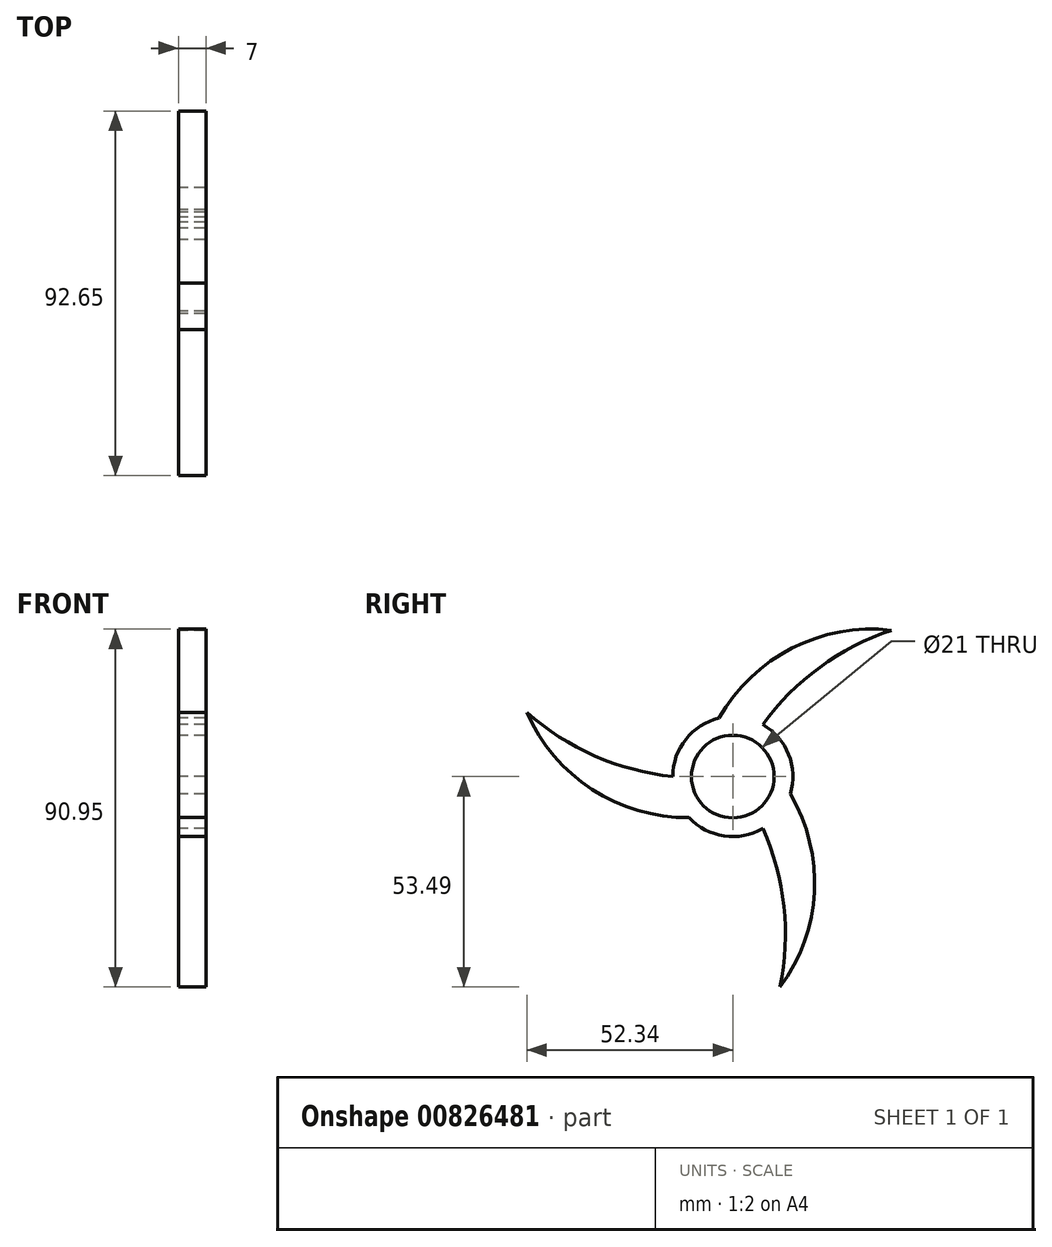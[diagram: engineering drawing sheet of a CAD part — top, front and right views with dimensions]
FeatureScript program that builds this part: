
annotation { "Feature Type Name" : "Feature", "Feature Type Description" : "" }
export const myFeature = defineFeature(function(context is Context, id is Id, definition is map)
    precondition{}
    {
        {
            var Q0;
            Q0=qCreatedBy(makeId("Right.planeOp"),FACE);
            var sketch = newSketch(context, id + "F0", { "sketchPlane" : qUnion([Q0])});
            skArc(sketch, "E0", {"start": v(-52.34, 16.33) * mm, "mid": v(-35.07, 5.26) * mm, "end": v(-15.25, 0) * mm});
            skArc(sketch, "E1", {"start": v(-52.34, 16.33) * mm, "mid": v(-35.78, -3.28) * mm, "end": v(-11.13, -10.42) * mm});
            skCircle(sketch, "E2", {"center": v(0, 0) * mm, "radius": 15.25 * mm});
            skCircle(sketch, "E3", {"center": v(0, 0) * mm, "radius": 10.5 * mm});
            skArc(sketch, "E4.1.0", {"start": v(12.03, -53.5) * mm, "mid": v(12.98, -33) * mm, "end": v(7.62, -13.2) * mm});
            skArc(sketch, "E4.1.1", {"start": v(12.03, -53.5) * mm, "mid": v(20.73, -29.35) * mm, "end": v(14.59, -4.43) * mm});
            skArc(sketch, "E4.2.0", {"start": v(40.31, 37.17) * mm, "mid": v(22.1, 27.74) * mm, "end": v(7.62, 13.2) * mm});
            skArc(sketch, "E4.2.1", {"start": v(40.31, 37.17) * mm, "mid": v(15.05, 32.63) * mm, "end": v(-3.46, 14.85) * mm});
            skSolve(sketch);
        }
        {
            var Q0;
            {var subQ0=sQuery(id+"F0.wireOp",EDGE,"E4.1.0");Q0=makeQuery(id+"F0.imprint","IMPRINT",FACE,{"disambiguationData":[TD([[makeQuery(id+"F0.imprint","IMPRINT",EDGE,{"derivedFrom":subQ0}),-1.0]])]});}
            var Q1;
            Q1=sQuery(id+"F0.wireOp",EDGE,"E4.1.0");
            var Q2;
            Q2=sQuery(id+"F0.wireOp",EDGE,"E4.1.1");
            extrude(context, id + "F1", {"entities" : qUnion([Q0]), "surfaceEntities" : qUnion([Q1, Q2]), "depth" : 7 * mm, "offsetDistance" : 25 * mm});
        }
        {
            var Q0;
            {var subQ0=sQuery(id+"F0.wireOp",EDGE,"E0");Q0=makeQuery(id+"F0.imprint","IMPRINT",FACE,{"disambiguationData":[TD([[makeQuery(id+"F0.imprint","IMPRINT",EDGE,{"derivedFrom":subQ0}),-1.0]])]});}
            var Q1;
            Q1=sQuery(id+"F0.wireOp",EDGE,"E0");
            var Q2;
            Q2=sQuery(id+"F0.wireOp",EDGE,"E1");
            extrude(context, id + "F2", {"entities" : qUnion([Q0]), "operationType" : NewBodyOperationType.ADD, "surfaceEntities" : qUnion([Q1, Q2]), "depth" : 7 * mm, "offsetDistance" : 25 * mm});
        }
        {
            var Q0;
            {var subQ0=sQuery(id+"F0.wireOp",EDGE,"E4.2.0");Q0=makeQuery(id+"F0.imprint","IMPRINT",FACE,{"disambiguationData":[TD([[makeQuery(id+"F0.imprint","IMPRINT",EDGE,{"derivedFrom":subQ0}),-1.0]])]});}
            var Q1;
            Q1=sQuery(id+"F0.wireOp",EDGE,"E4.2.0");
            var Q2;
            Q2=sQuery(id+"F0.wireOp",EDGE,"E4.2.1");
            extrude(context, id + "F3", {"entities" : qUnion([Q0]), "operationType" : NewBodyOperationType.ADD, "surfaceEntities" : qUnion([Q1, Q2]), "depth" : 7 * mm, "offsetDistance" : 25 * mm});
        }
        {
            var Q0;
            Q0=makeQuery(id+"F0.imprint","IMPRINT",FACE,{"disambiguationData":[TD([[makeQuery(id+"F0.imprint","IMPRINT",EDGE,{"derivedFrom":sQuery(id+"F0.wireOp",EDGE,"E3")}),-1.0]])]});
            var Q1;
            Q1=sQuery(id+"F0.wireOp",EDGE,"E2");
            var Q2;
            Q2=sQuery(id+"F0.wireOp",EDGE,"E3");
            extrude(context, id + "F4", {"entities" : qUnion([Q0]), "operationType" : NewBodyOperationType.ADD, "surfaceEntities" : qUnion([Q1, Q2]), "depth" : 7 * mm, "offsetDistance" : 25 * mm});
        }
    });
